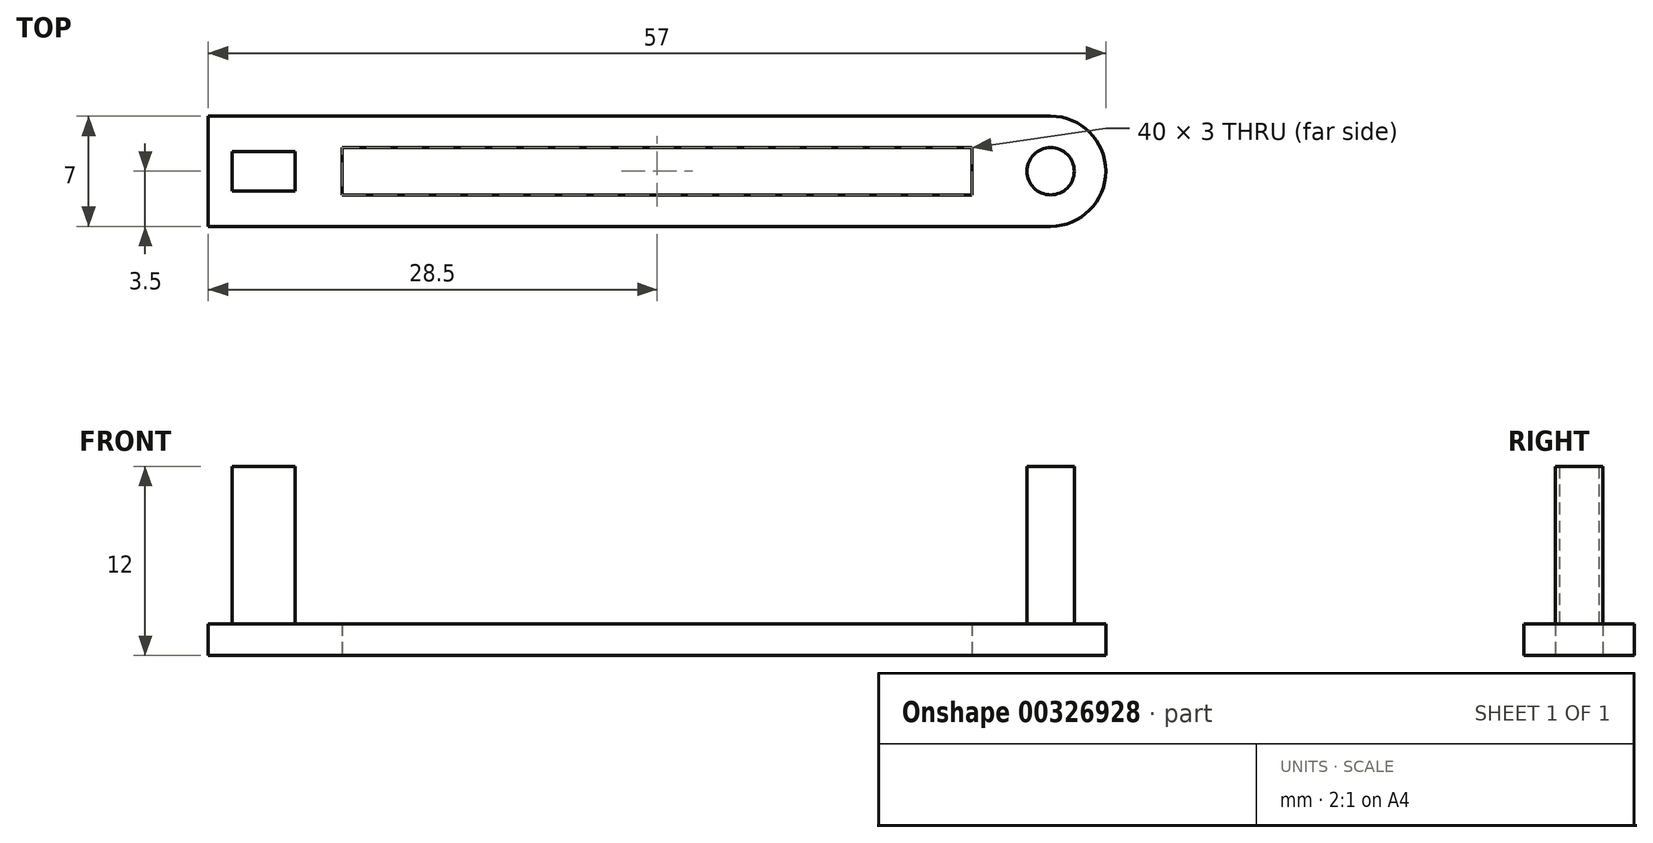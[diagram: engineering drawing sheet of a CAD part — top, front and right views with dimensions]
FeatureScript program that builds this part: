
annotation { "Feature Type Name" : "Feature", "Feature Type Description" : "" }
export const myFeature = defineFeature(function(context is Context, id is Id, definition is map)
    precondition{}
    {
        {
            var Q0;
            Q0=qCreatedBy(makeId("Top.planeOp"),FACE);
            var sketch = newSketch(context, id + "F0", { "sketchPlane" : qUnion([Q0])});
            skLineSegment(sketch, "E0", {"start": v(0, 0) * mm, "end": v(50, 0) * mm});
            skCircle(sketch, "E1", {"center": v(50, 0) * mm, "radius": 1.5 * mm});
            skCircle(sketch, "E2", {"center": v(50, 0) * mm, "radius": 3.5 * mm});
            skLineSegment(sketch, "E3", {"start": v(50, 3.5) * mm, "end": v(0, 3.5) * mm});
            skLineSegment(sketch, "E4", {"start": v(50, -3.5) * mm, "end": v(0, -3.5) * mm});
            skLineSegment(sketch, "E5.bottom", {"start": v(3.5, -3.5) * mm, "end": v(-3.5, -3.5) * mm});
            skLineSegment(sketch, "E5.top", {"start": v(3.5, 3.5) * mm, "end": v(-3.5, 3.5) * mm});
            skLineSegment(sketch, "E5.left", {"start": v(3.5, -3.5) * mm, "end": v(3.5, 3.5) * mm});
            skLineSegment(sketch, "E5.right", {"start": v(-3.5, -3.5) * mm, "end": v(-3.5, 3.5) * mm});
            skPoint(sketch, "E5.middle", {"position": v(0, 0) * mm});
            skLineSegment(sketch, "E6.bottom", {"start": v(2, -1.25) * mm, "end": v(-2, -1.25) * mm});
            skLineSegment(sketch, "E6.top", {"start": v(2, 1.25) * mm, "end": v(-2, 1.25) * mm});
            skLineSegment(sketch, "E6.left", {"start": v(2, -1.25) * mm, "end": v(2, 1.25) * mm});
            skLineSegment(sketch, "E6.right", {"start": v(-2, -1.25) * mm, "end": v(-2, 1.25) * mm});
            skLineSegment(sketch, "E7.bottom", {"start": v(45, -1.5) * mm, "end": v(5, -1.5) * mm});
            skLineSegment(sketch, "E7.top", {"start": v(45, 1.5) * mm, "end": v(5, 1.5) * mm});
            skLineSegment(sketch, "E7.left", {"start": v(45, -1.5) * mm, "end": v(45, 1.5) * mm});
            skLineSegment(sketch, "E7.right", {"start": v(5, -1.5) * mm, "end": v(5, 1.5) * mm});
            skPoint(sketch, "E7.middle", {"position": v(25, 0) * mm});
            skSolve(sketch);
        }
        {
            var Q0;
            {var subQ0=sQuery(id+"F0.wireOp",EDGE,"E3");Q0=makeQuery(id+"F0.imprint","IMPRINT",FACE,{"disambiguationData":[TD([[makeQuery(id+"F0.imprint","IMPRINT",EDGE,{"derivedFrom":subQ0}),1.0]])]});}
            var Q1;
            {var subQ0=sQuery(id+"F0.wireOp",EDGE,"E4");Q1=makeQuery(id+"F0.imprint","IMPRINT",FACE,{"disambiguationData":[TD([[makeQuery(id+"F0.imprint","IMPRINT",EDGE,{"derivedFrom":subQ0}),-1.0]])]});}
            var Q2;
            {var subQ6=sQuery(id+"F0.wireOp",EDGE,"E5.right");Q2=makeQuery(id+"F0.imprint","IMPRINT",FACE,{"disambiguationData":[TD([[makeQuery(id+"F0.imprint","IMPRINT",EDGE,{"derivedFrom":subQ6}),-1.0]])]});}
            var Q3;
            {var subQ3=sQuery(id+"F0.wireOp",EDGE,"E6.bottom");Q3=makeQuery(id+"F0.imprint","IMPRINT",FACE,{"disambiguationData":[TD([[makeQuery(id+"F0.imprint","IMPRINT",EDGE,{"derivedFrom":subQ3}),-1.0]])]});}
            var Q4;
            Q4=makeQuery(id+"F0.imprint","IMPRINT",FACE,{"disambiguationData":[TD([[makeQuery(id+"F0.imprint","IMPRINT",EDGE,{"derivedFrom":sQuery(id+"F0.wireOp",EDGE,"E1")}),-1.0]])]});
            var Q5;
            Q5=makeQuery(id+"F0.imprint","IMPRINT",FACE,{"disambiguationData":[TD([[makeQuery(id+"F0.imprint","IMPRINT",EDGE,{"derivedFrom":sQuery(id+"F0.wireOp",EDGE,"E1")}),1.0]])]});
            extrude(context, id + "F1", {"entities" : qUnion([Q0, Q1, Q2, Q3, Q4, Q5]), "depth" : 2 * mm});
        }
        {
            var Q0;
            {var subQ3=sQuery(id+"F0.wireOp",EDGE,"E6.bottom");Q0=makeQuery(id+"F0.imprint","IMPRINT",FACE,{"disambiguationData":[TD([[makeQuery(id+"F0.imprint","IMPRINT",EDGE,{"derivedFrom":subQ3}),-1.0]])]});}
            extrude(context, id + "F2", {"entities" : qUnion([Q0]), "operationType" : NewBodyOperationType.ADD, "depth" : 12 * mm});
        }
        {
            var Q0;
            Q0=makeQuery(id+"F0.imprint","IMPRINT",FACE,{"disambiguationData":[TD([[makeQuery(id+"F0.imprint","IMPRINT",EDGE,{"derivedFrom":sQuery(id+"F0.wireOp",EDGE,"E1")}),1.0]])]});
            extrude(context, id + "F3", {"entities" : qUnion([Q0]), "operationType" : NewBodyOperationType.ADD, "depth" : 12 * mm});
        }
    });
